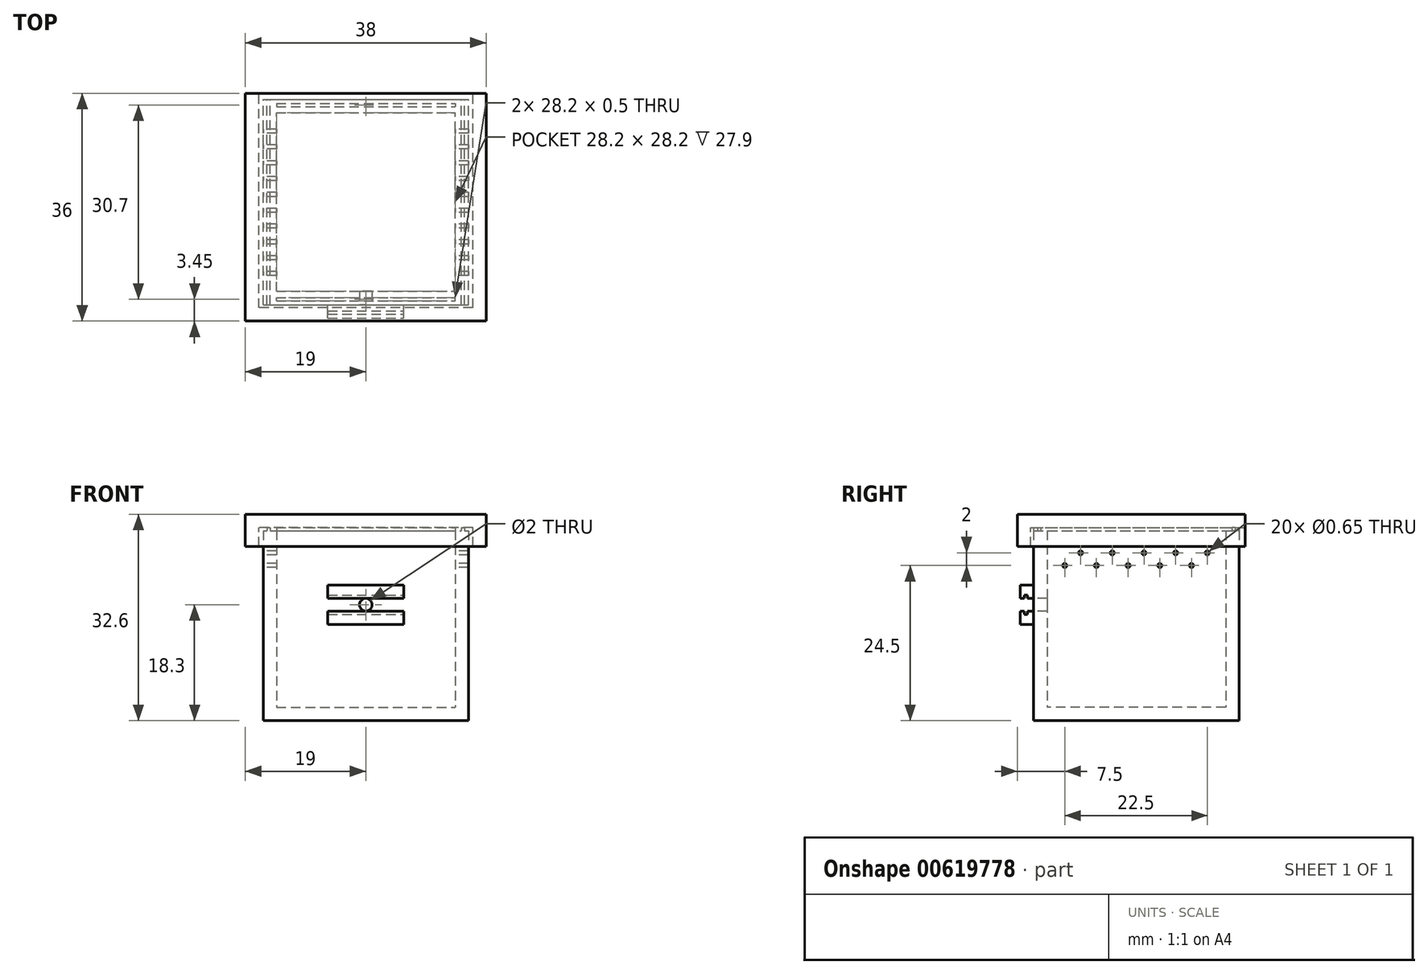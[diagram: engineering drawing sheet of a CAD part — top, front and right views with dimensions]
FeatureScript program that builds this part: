
annotation { "Feature Type Name" : "Feature", "Feature Type Description" : "" }
export const myFeature = defineFeature(function(context is Context, id is Id, definition is map)
    precondition{}
    {
        {
            var Q0;
            Q0=qCreatedBy(makeId("Top.planeOp"),FACE);
            var sketch = newSketch(context, id + "F0", { "sketchPlane" : qUnion([Q0])});
            skLineSegment(sketch, "E0.bottom", {"start": v(-14.1, 14.1) * mm, "end": v(14.1, 14.1) * mm});
            skLineSegment(sketch, "E0.top", {"start": v(-14.1, -14.1) * mm, "end": v(14.1, -14.1) * mm});
            skLineSegment(sketch, "E0.left", {"start": v(14.1, 14.1) * mm, "end": v(14.1, -14.1) * mm});
            skLineSegment(sketch, "E0.right", {"start": v(-14.1, 14.1) * mm, "end": v(-14.1, -14.1) * mm});
            skLineSegment(sketch, "E1.bottom", {"start": v(-14.1, 14.1) * mm, "end": v(-0.1, 14.1) * mm, "construction": true});
            skLineSegment(sketch, "E1.top", {"start": v(-14.1, 7.1) * mm, "end": v(-0.1, 7.1) * mm, "construction": true});
            skLineSegment(sketch, "E1.left", {"start": v(-14.1, 14.1) * mm, "end": v(-14.1, 7.1) * mm, "construction": true});
            skLineSegment(sketch, "E1.right", {"start": v(-0.1, 14.1) * mm, "end": v(-0.1, 7.1) * mm, "construction": true});
            skLineSegment(sketch, "E2.0.1.0", {"start": v(-14.1, 7.1) * mm, "end": v(-14.1, 0.1) * mm, "construction": true});
            skLineSegment(sketch, "E2.0.1.1", {"start": v(-14.1, 0.1) * mm, "end": v(-0.1, 0.1) * mm, "construction": true});
            skLineSegment(sketch, "E2.0.1.2", {"start": v(-0.1, 7.1) * mm, "end": v(-0.1, 0.1) * mm, "construction": true});
            skLineSegment(sketch, "E2.1.0.1", {"start": v(-0.1, 7.1) * mm, "end": v(13.9, 7.1) * mm, "construction": true});
            skLineSegment(sketch, "E2.1.0.2", {"start": v(13.9, 14.1) * mm, "end": v(13.9, 7.1) * mm, "construction": true});
            skLineSegment(sketch, "E2.1.0.3", {"start": v(-0.1, 14.1) * mm, "end": v(13.9, 14.1) * mm, "construction": true});
            skLineSegment(sketch, "E2.1.1.0", {"start": v(-0.1, 7.1) * mm, "end": v(-0.1, 0.1) * mm, "construction": true});
            skLineSegment(sketch, "E2.1.1.1", {"start": v(-0.1, 0.1) * mm, "end": v(13.9, 0.1) * mm, "construction": true});
            skLineSegment(sketch, "E2.1.1.2", {"start": v(13.9, 7.1) * mm, "end": v(13.9, 0.1) * mm, "construction": true});
            skLineSegment(sketch, "E2.1.1.3", {"start": v(-0.1, 7.1) * mm, "end": v(13.9, 7.1) * mm, "construction": true});
            skLineSegment(sketch, "E2.direction2", {"start": v(-14.1, 7.1) * mm, "end": v(-14.1, 0.1) * mm, "construction": true});
            skLineSegment(sketch, "E3.0.0.2", {"start": v(-14.1, 0.1) * mm, "end": v(-14.1, -6.9) * mm, "construction": true});
            skLineSegment(sketch, "E3.3.0.2", {"start": v(-14.1, -6.9) * mm, "end": v(-0.1, -6.9) * mm, "construction": true});
            skLineSegment(sketch, "E3.6.0.2", {"start": v(-0.1, 0.1) * mm, "end": v(-0.1, -6.9) * mm, "construction": true});
            skLineSegment(sketch, "E3.0.1.2", {"start": v(-0.1, 0.1) * mm, "end": v(-0.1, -6.9) * mm, "construction": true});
            skLineSegment(sketch, "E3.3.1.2", {"start": v(-0.1, -6.9) * mm, "end": v(13.9, -6.9) * mm, "construction": true});
            skLineSegment(sketch, "E3.6.1.2", {"start": v(13.9, 0.1) * mm, "end": v(13.9, -6.9) * mm, "construction": true});
            skLineSegment(sketch, "E4.0.0.3", {"start": v(-14.1, -6.9) * mm, "end": v(-14.1, -13.9) * mm, "construction": true});
            skLineSegment(sketch, "E4.3.0.3", {"start": v(-14.1, -13.9) * mm, "end": v(-0.1, -13.9) * mm, "construction": true});
            skLineSegment(sketch, "E4.6.0.3", {"start": v(-0.1, -6.9) * mm, "end": v(-0.1, -13.9) * mm, "construction": true});
            skLineSegment(sketch, "E4.0.1.3", {"start": v(-0.1, -6.9) * mm, "end": v(-0.1, -13.9) * mm, "construction": true});
            skLineSegment(sketch, "E4.3.1.3", {"start": v(-0.1, -13.9) * mm, "end": v(13.9, -13.9) * mm, "construction": true});
            skLineSegment(sketch, "E4.6.1.3", {"start": v(13.9, -6.9) * mm, "end": v(13.9, -13.9) * mm, "construction": true});
            skSolve(sketch);
        }
        {
            var Q0;
            Q0=qCreatedBy(makeId("Top.planeOp"),FACE);
            var sketch = newSketch(context, id + "F1", { "sketchPlane" : qUnion([Q0])});
            skLineSegment(sketch, "E5.bottom", {"start": v(-16.2, -16.2) * mm, "end": v(-14.1, -16.2) * mm});
            skLineSegment(sketch, "E5.top", {"start": v(-16.2, 16.2) * mm, "end": v(-14.1, 16.2) * mm});
            skLineSegment(sketch, "E5.left", {"start": v(-16.2, -16.2) * mm, "end": v(-16.2, 16.2) * mm});
            skLineSegment(sketch, "E5.right", {"start": v(-14.1, -16.2) * mm, "end": v(-14.1, 16.2) * mm});
            skLineSegment(sketch, "E6.bottom", {"start": v(-14.1, 14.1) * mm, "end": v(14.1, 14.1) * mm});
            skLineSegment(sketch, "E6.top", {"start": v(-14.1, 16.2) * mm, "end": v(14.1, 16.2) * mm});
            skLineSegment(sketch, "E6.left", {"start": v(-14.1, 14.1) * mm, "end": v(-14.1, 16.2) * mm});
            skLineSegment(sketch, "E6.right", {"start": v(14.1, 14.1) * mm, "end": v(14.1, 16.2) * mm});
            skLineSegment(sketch, "E7.MirrorCS", {"start": v(-14.1, -14.1) * mm, "end": v(-14.1, -16.2) * mm});
            skLineSegment(sketch, "E8.MirrorCS", {"start": v(-14.1, -16.2) * mm, "end": v(14.1, -16.2) * mm});
            skLineSegment(sketch, "E9.MirrorCS", {"start": v(-14.1, -14.1) * mm, "end": v(14.1, -14.1) * mm});
            skLineSegment(sketch, "E10.MirrorCS", {"start": v(14.1, -14.1) * mm, "end": v(14.1, -16.2) * mm});
            skLineSegment(sketch, "E11.MirrorCS", {"start": v(16.2, 16.2) * mm, "end": v(14.1, 16.2) * mm});
            skLineSegment(sketch, "E12.MirrorCS", {"start": v(14.1, -16.2) * mm, "end": v(14.1, 16.2) * mm});
            skLineSegment(sketch, "E13.MirrorCS", {"start": v(16.2, -16.2) * mm, "end": v(16.2, 16.2) * mm});
            skLineSegment(sketch, "E14.MirrorCS", {"start": v(16.2, -16.2) * mm, "end": v(14.1, -16.2) * mm});
            skSolve(sketch);
        }
        {
            var Q0;
            Q0 = qSketchRegion(id + "F0", true);
            extrude(context, id + "F2", {"entities" : qUnion([Q0]), "depth" : 2.1 * mm, "offsetDistance" : 25 * mm});
        }
        {
            var Q0;
            Q0 = qSketchRegion(id + "F1", true);
            extrude(context, id + "F3", {"entities" : qUnion([Q0]), "operationType" : NewBodyOperationType.ADD, "depth" : 30 * mm, "offsetDistance" : 25 * mm});
        }
        {
            var Q0;
            Q0=makeQuery(id+"F3.opExtrude","CAP_FACE",FACE,{"disambiguationData":[OSD([sQuery(id+"F1.wireOp",EDGE,"E5.bottom"),sQuery(id+"F1.wireOp",EDGE,"E5.top"),sQuery(id+"F1.wireOp",EDGE,"E5.left"),sQuery(id+"F1.wireOp",EDGE,"E5.right"),sQuery(id+"F1.wireOp",EDGE,"E6.bottom"),sQuery(id+"F1.wireOp",EDGE,"E6.top"),sQuery(id+"F1.wireOp",EDGE,"E8.MirrorCS"),sQuery(id+"F1.wireOp",EDGE,"E9.MirrorCS"),sQuery(id+"F1.wireOp",EDGE,"E11.MirrorCS"),sQuery(id+"F1.wireOp",EDGE,"E12.MirrorCS"),sQuery(id+"F1.wireOp",EDGE,"E13.MirrorCS"),sQuery(id+"F1.wireOp",EDGE,"E14.MirrorCS")])],"isStart":false});
            var sketch = newSketch(context, id + "F4", { "sketchPlane" : qUnion([Q0])});
            skLineSegment(sketch, "E15.bottom", {"start": v(-15.6, -16.2) * mm, "end": v(-15.1, -16.2) * mm});
            skLineSegment(sketch, "E15.top", {"start": v(-15.6, 16.2) * mm, "end": v(-15.1, 16.2) * mm});
            skLineSegment(sketch, "E15.left", {"start": v(-15.6, -16.2) * mm, "end": v(-15.6, 16.2) * mm});
            skLineSegment(sketch, "E15.right", {"start": v(-15.1, -16.2) * mm, "end": v(-15.1, 16.2) * mm});
            skLineSegment(sketch, "E16.MirrorCS", {"start": v(15.6, 16.2) * mm, "end": v(15.1, 16.2) * mm});
            skLineSegment(sketch, "E17.MirrorCS", {"start": v(15.1, -16.2) * mm, "end": v(15.1, 16.2) * mm});
            skLineSegment(sketch, "E18.MirrorCS", {"start": v(15.6, -16.2) * mm, "end": v(15.1, -16.2) * mm});
            skLineSegment(sketch, "E19.MirrorCS", {"start": v(15.6, -16.2) * mm, "end": v(15.6, 16.2) * mm});
            skLineSegment(sketch, "E20.bottom", {"start": v(-14.1, 15.6) * mm, "end": v(14.1, 15.6) * mm});
            skLineSegment(sketch, "E20.top", {"start": v(-14.1, 15.1) * mm, "end": v(14.1, 15.1) * mm});
            skLineSegment(sketch, "E20.left", {"start": v(-14.1, 15.6) * mm, "end": v(-14.1, 15.1) * mm});
            skLineSegment(sketch, "E20.right", {"start": v(14.1, 15.6) * mm, "end": v(14.1, 15.1) * mm});
            skLineSegment(sketch, "E21", {"start": v(-14.1, 14.1) * mm, "end": v(-14.1, 16.2) * mm, "construction": true});
            skLineSegment(sketch, "E22.MirrorCS", {"start": v(-14.1, -15.6) * mm, "end": v(14.1, -15.6) * mm});
            skLineSegment(sketch, "E23.MirrorCS", {"start": v(14.1, -15.6) * mm, "end": v(14.1, -15.1) * mm});
            skLineSegment(sketch, "E24.MirrorCS", {"start": v(-14.1, -15.1) * mm, "end": v(14.1, -15.1) * mm});
            skLineSegment(sketch, "E25", {"start": v(-14.1, -15.6) * mm, "end": v(-14.1, -15.1) * mm});
            skSolve(sketch);
        }
        {
            var Q0;
            Q0 = qSketchRegion(id + "F4", true);
            extrude(context, id + "F5", {"entities" : qUnion([Q0]), "operationType" : NewBodyOperationType.ADD, "depth" : 0.5 * mm, "offsetDistance" : 25 * mm});
        }
        {
            var Q0;
            Q0=makeQuery(id+"F5.opExtrude","CAP_FACE",FACE,{"disambiguationData":[OSD([sQuery(id+"F4.wireOp",EDGE,"E15.bottom"),sQuery(id+"F4.wireOp",EDGE,"E15.top"),sQuery(id+"F4.wireOp",EDGE,"E15.left"),sQuery(id+"F4.wireOp",EDGE,"E15.right")])],"isStart":false});
            var sketch = newSketch(context, id + "F6", { "sketchPlane" : qUnion([Q0])});
            skLineSegment(sketch, "E26.bottom", {"start": v(-19, 17.2) * mm, "end": v(19, 17.2) * mm});
            skLineSegment(sketch, "E26.top", {"start": v(-19, -18.8) * mm, "end": v(19, -18.8) * mm});
            skLineSegment(sketch, "E26.left", {"start": v(-19, 17.2) * mm, "end": v(-19, -18.8) * mm});
            skLineSegment(sketch, "E26.right", {"start": v(19, 17.2) * mm, "end": v(19, -18.8) * mm});
            skLineSegment(sketch, "E27", {"start": v(-3.5, 17.2) * mm, "end": v(-3.5, -18.8) * mm});
            skLineSegment(sketch, "E28", {"start": v(12, 17.2) * mm, "end": v(12, -18.8) * mm});
            skSolve(sketch);
        }
        {
            var Q0;
            Q0 = qSketchRegion(id + "F6", true);
            extrude(context, id + "F7", {"entities" : qUnion([Q0]), "operationType" : NewBodyOperationType.ADD, "depth" : 2.1 * mm, "offsetDistance" : 25 * mm});
        }
        {
            var Q0;
            Q0=makeQuery(id+"F5.boolean.opBoolean","MERGE",FACE,{"derivedFrom":[makeQuery(id+"F3.opExtrude","SWEPT_FACE",FACE,{"disambiguationData":[OSD([sQuery(id+"F1.wireOp",EDGE,"E5.bottom"),sQuery(id+"F1.wireOp",EDGE,"E8.MirrorCS"),sQuery(id+"F1.wireOp",EDGE,"E14.MirrorCS")])]}),makeQuery(id+"F5.opExtrude","SWEPT_FACE",FACE,{"disambiguationData":[OSD([sQuery(id+"F4.wireOp",EDGE,"E15.bottom")])]}),makeQuery(id+"F5.opExtrude","SWEPT_FACE",FACE,{"disambiguationData":[OSD([sQuery(id+"F4.wireOp",EDGE,"E18.MirrorCS")])]})]});
            var sketch = newSketch(context, id + "F8", { "sketchPlane" : qUnion([Q0])});
            skCircle(sketch, "E29", {"center": v(0, 18.3) * mm, "radius": 1 * mm});
            skLineSegment(sketch, "E30.bottom", {"start": v(-6, 17.3) * mm, "end": v(6, 17.3) * mm});
            skLineSegment(sketch, "E30.top", {"start": v(-6, 15.2) * mm, "end": v(6, 15.2) * mm});
            skLineSegment(sketch, "E30.left", {"start": v(-6, 17.3) * mm, "end": v(-6, 15.2) * mm});
            skLineSegment(sketch, "E30.right", {"start": v(6, 17.3) * mm, "end": v(6, 15.2) * mm});
            skLineSegment(sketch, "E31", {"start": v(-16.2, 18.3) * mm, "end": v(16.2, 18.3) * mm, "construction": true});
            skLineSegment(sketch, "E32.MirrorCS", {"start": v(6, 19.3) * mm, "end": v(6, 21.4) * mm});
            skLineSegment(sketch, "E33.MirrorCS", {"start": v(-6, 21.4) * mm, "end": v(6, 21.4) * mm});
            skLineSegment(sketch, "E34.MirrorCS", {"start": v(-6, 19.3) * mm, "end": v(-6, 21.4) * mm});
            skLineSegment(sketch, "E35.MirrorCS", {"start": v(-6, 19.3) * mm, "end": v(6, 19.3) * mm});
            skSolve(sketch);
        }
        {
            var Q0;
            Q0=makeQuery(id+"F8.imprint","IMPRINT",FACE,{"disambiguationData":[TD([[makeQuery(id+"F8.imprint","IMPRINT",EDGE,{"derivedFrom":sQuery(id+"F8.wireOp",EDGE,"E29")}),1.0]])]});
            extrude(context, id + "F9", {"entities" : qUnion([Q0]), "operationType" : NewBodyOperationType.REMOVE, "endBound" : BoundingType.UP_TO_NEXT, "oppositeDirection" : true, "depth" : 25 * mm, "offsetDistance" : 25 * mm});
        }
        {
            var Q0;
            Q0=makeQuery(id+"F8.imprint","IMPRINT",FACE,{"disambiguationData":[TD([[makeQuery(id+"F8.imprint","IMPRINT",EDGE,{"derivedFrom":sQuery(id+"F8.wireOp",EDGE,"E30.bottom")}),-1.0]])]});
            var Q1;
            Q1=makeQuery(id+"F8.imprint","IMPRINT",FACE,{"disambiguationData":[TD([[makeQuery(id+"F8.imprint","IMPRINT",EDGE,{"derivedFrom":sQuery(id+"F8.wireOp",EDGE,"E32.MirrorCS")}),1.0]])]});
            extrude(context, id + "F10", {"entities" : qUnion([Q0, Q1]), "operationType" : NewBodyOperationType.ADD, "depth" : 2.1 * mm, "offsetDistance" : 25 * mm});
        }
        {
            var Q0;
            {var subQ0=sQuery(id+"F6.wireOp",EDGE,"E26.right");Q0=makeQuery(id+"F6.imprint","IMPRINT",FACE,{"disambiguationData":[TD([[makeQuery(id+"F6.imprint","IMPRINT",EDGE,{"derivedFrom":subQ0}),-1.0]])]});}
            var sketch = newSketch(context, id + "F11", { "sketchPlane" : qUnion([Q0])});
            skLineSegment(sketch, "E36.bottom", {"start": v(16.9, -18.8) * mm, "end": v(19, -18.8) * mm});
            skLineSegment(sketch, "E36.top", {"start": v(16.9, 17.2) * mm, "end": v(19, 17.2) * mm});
            skLineSegment(sketch, "E36.left", {"start": v(16.9, -18.8) * mm, "end": v(16.9, 17.2) * mm});
            skLineSegment(sketch, "E36.right", {"start": v(19, -18.8) * mm, "end": v(19, 17.2) * mm});
            skLineSegment(sketch, "E37.MirrorCS", {"start": v(-16.9, -18.8) * mm, "end": v(-19, -18.8) * mm});
            skLineSegment(sketch, "E38.MirrorCS", {"start": v(-19, -18.8) * mm, "end": v(-19, 17.2) * mm});
            skLineSegment(sketch, "E39.MirrorCS", {"start": v(-16.9, -18.8) * mm, "end": v(-16.9, 17.2) * mm});
            skLineSegment(sketch, "E40.MirrorCS", {"start": v(-16.9, 17.2) * mm, "end": v(-19, 17.2) * mm});
            skLineSegment(sketch, "E41.bottom", {"start": v(16.9, -18.8) * mm, "end": v(-16.9, -18.8) * mm});
            skLineSegment(sketch, "E41.top", {"start": v(16.9, -16.7) * mm, "end": v(-16.9, -16.7) * mm});
            skLineSegment(sketch, "E41.left", {"start": v(16.9, -18.8) * mm, "end": v(16.9, -16.7) * mm});
            skLineSegment(sketch, "E41.right", {"start": v(-16.9, -18.8) * mm, "end": v(-16.9, -16.7) * mm});
            skSolve(sketch);
        }
        {
            var Q0;
            Q0 = qSketchRegion(id + "F11", true);
            extrude(context, id + "F12", {"entities" : qUnion([Q0]), "operationType" : NewBodyOperationType.ADD, "oppositeDirection" : true, "depth" : 3 * mm, "offsetDistance" : 25 * mm});
        }
        {
            var Q0;
            Q0=makeQuery(id+"F3.opExtrude","SWEPT_FACE",FACE,{"disambiguationData":[OSD([sQuery(id+"F1.wireOp",EDGE,"E5.left")])]});
            var sketch = newSketch(context, id + "F13", { "sketchPlane" : qUnion([Q0])});
            skLineSegment(sketch, "E42", {"start": v(-16.2, 26.5) * mm, "end": v(16.2, 26.5) * mm, "construction": true});
            skLineSegment(sketch, "E43", {"start": v(-16.2, 24.5) * mm, "end": v(16.2, 24.5) * mm, "construction": true});
            skCircle(sketch, "E44", {"center": v(-11.2, 26.5) * mm, "radius": 0.33 * mm});
            skCircle(sketch, "E45", {"center": v(-8.7, 24.5) * mm, "radius": 0.33 * mm});
            skCircle(sketch, "E46.1.0.0", {"center": v(-6.2, 26.5) * mm, "radius": 0.33 * mm});
            skCircle(sketch, "E46.1.0.1", {"center": v(-3.7, 24.5) * mm, "radius": 0.33 * mm});
            skCircle(sketch, "E46.2.0.0", {"center": v(-1.2, 26.5) * mm, "radius": 0.33 * mm});
            skCircle(sketch, "E46.2.0.1", {"center": v(1.3, 24.5) * mm, "radius": 0.33 * mm});
            skCircle(sketch, "E46.3.0.0", {"center": v(3.8, 26.5) * mm, "radius": 0.33 * mm});
            skCircle(sketch, "E46.3.0.1", {"center": v(6.3, 24.5) * mm, "radius": 0.33 * mm});
            skCircle(sketch, "E46.4.0.0", {"center": v(8.8, 26.5) * mm, "radius": 0.33 * mm});
            skCircle(sketch, "E46.4.0.1", {"center": v(11.3, 24.5) * mm, "radius": 0.33 * mm});
            skLineSegment(sketch, "E46.direction1", {"start": v(-11.2, 26.5) * mm, "end": v(-6.2, 26.5) * mm, "construction": true});
            skSolve(sketch);
        }
        {
            var Q0;
            Q0 = qSketchRegion(id + "F13", true);
            extrude(context, id + "F14", {"entities" : qUnion([Q0]), "operationType" : NewBodyOperationType.REMOVE, "endBound" : BoundingType.THROUGH_ALL, "oppositeDirection" : true, "depth" : 25 * mm, "offsetDistance" : 25 * mm});
        }
        {
            var Q0;
            Q0=makeQuery(id+"F10.opExtrude","SWEPT_FACE",FACE,{"disambiguationData":[OSD([sQuery(id+"F8.wireOp",EDGE,"E30.right")])]});
            var sketch = newSketch(context, id + "F15", { "sketchPlane" : qUnion([Q0])});
            skLineSegment(sketch, "E47.bottom", {"start": v(-17.7, 17.3) * mm, "end": v(-17.2, 17.3) * mm});
            skLineSegment(sketch, "E47.top", {"start": v(-17.7, 16.8) * mm, "end": v(-17.2, 16.8) * mm});
            skLineSegment(sketch, "E47.left", {"start": v(-17.7, 17.3) * mm, "end": v(-17.7, 16.8) * mm});
            skLineSegment(sketch, "E47.right", {"start": v(-17.2, 17.3) * mm, "end": v(-17.2, 16.8) * mm});
            skLineSegment(sketch, "E48.bottom", {"start": v(-17.7, 19.3) * mm, "end": v(-17.2, 19.3) * mm});
            skLineSegment(sketch, "E48.top", {"start": v(-17.7, 19.8) * mm, "end": v(-17.2, 19.8) * mm});
            skLineSegment(sketch, "E48.left", {"start": v(-17.7, 19.3) * mm, "end": v(-17.7, 19.8) * mm});
            skLineSegment(sketch, "E48.right", {"start": v(-17.2, 19.3) * mm, "end": v(-17.2, 19.8) * mm});
            skSolve(sketch);
        }
        {
            var Q0;
            Q0 = qSketchRegion(id + "F15", true);
            extrude(context, id + "F16", {"entities" : qUnion([Q0]), "operationType" : NewBodyOperationType.REMOVE, "endBound" : BoundingType.THROUGH_ALL, "oppositeDirection" : true, "depth" : 25 * mm, "offsetDistance" : 25 * mm});
        }
    });
